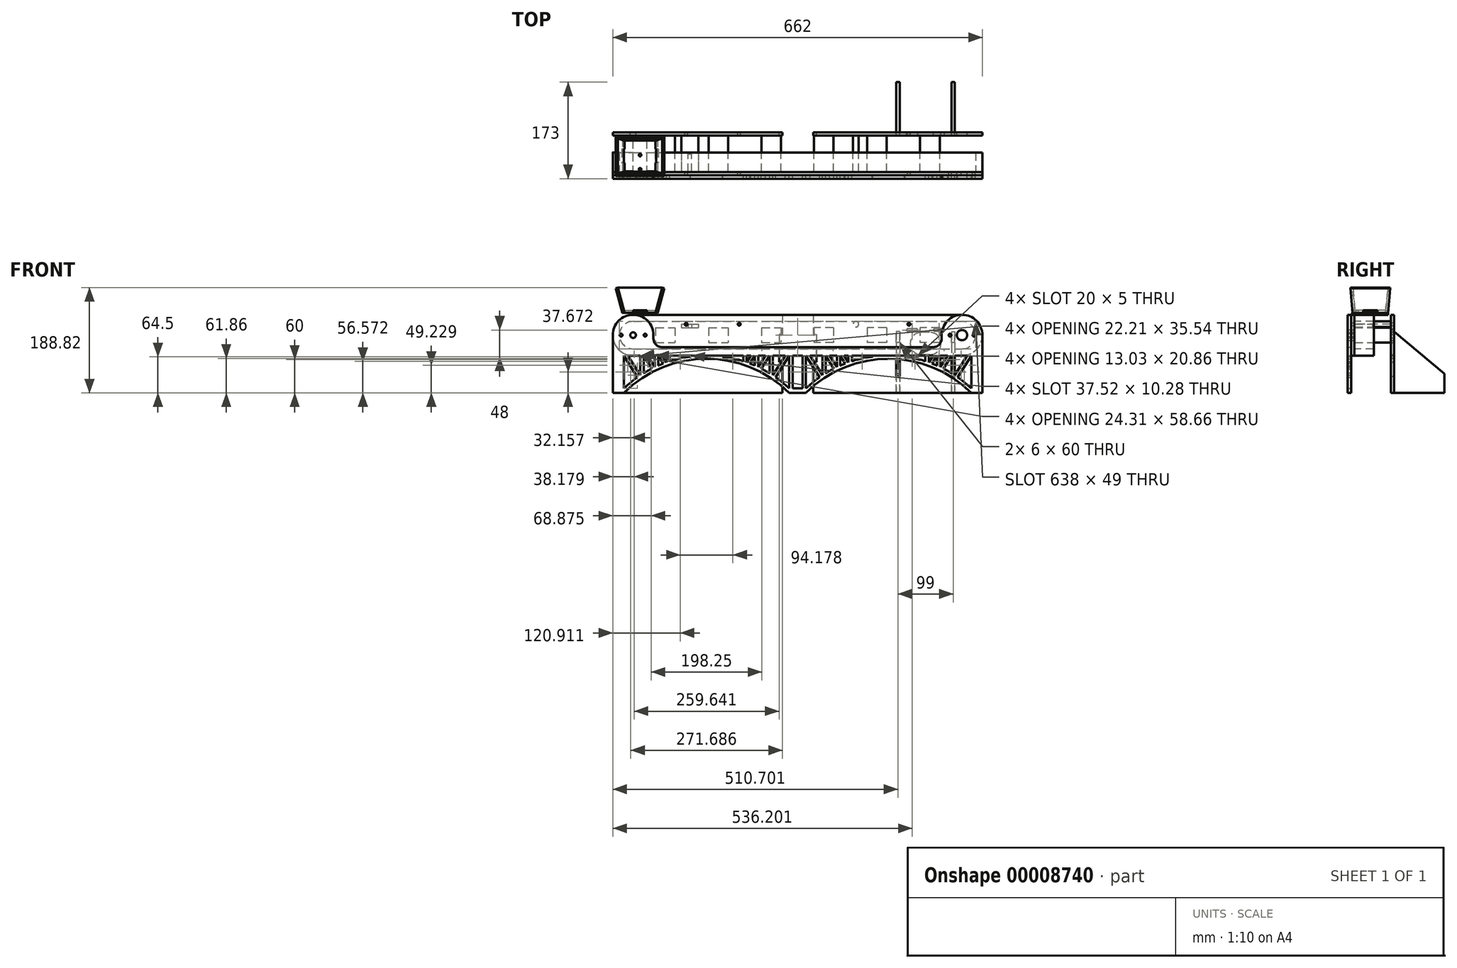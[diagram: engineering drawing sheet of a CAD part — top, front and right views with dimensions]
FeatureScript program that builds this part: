
annotation { "Feature Type Name" : "Feature", "Feature Type Description" : "" }
export const myFeature = defineFeature(function(context is Context, id is Id, definition is map)
    precondition{}
    {
        {
            var Q0;
            Q0=qCreatedBy(makeId("Front.planeOp"),FACE);
            var sketch = newSketch(context, id + "F0", { "sketchPlane" : qUnion([Q0])});
            skLineSegment(sketch, "E0.bottom", {"start": v(331, 0) * mm, "end": v(-331, 0) * mm, "construction": true});
            skLineSegment(sketch, "E0.top", {"start": v(331, 140) * mm, "end": v(-331, 140) * mm, "construction": true});
            skLineSegment(sketch, "E0.left", {"start": v(331, 0) * mm, "end": v(331, 140) * mm, "construction": true});
            skLineSegment(sketch, "E0.right", {"start": v(-331, 0) * mm, "end": v(-331, 140) * mm, "construction": true});
            skCircle(sketch, "E1", {"center": v(-294.5, 103.5) * mm, "radius": 36.5 * mm, "construction": true});
            skCircle(sketch, "E2", {"center": v(-294.5, 103.5) * mm, "radius": 24.5 * mm, "construction": true});
            skLineSegment(sketch, "E3", {"start": v(0, 0) * mm, "end": v(0, 140) * mm, "construction": true});
            skCircle(sketch, "E4.0.MirrorC", {"center": v(294.5, 103.5) * mm, "radius": 36.5 * mm, "construction": true});
            skCircle(sketch, "E5.0.MirrorC", {"center": v(294.5, 103.5) * mm, "radius": 24.5 * mm, "construction": true});
            skLineSegment(sketch, "E6", {"start": v(-294.5, 128) * mm, "end": v(294.5, 128) * mm, "construction": true});
            skCircle(sketch, "E7", {"center": v(-199.5, 123) * mm, "radius": 5 * mm, "construction": true});
            skCircle(sketch, "E8", {"center": v(-104.5, 123) * mm, "radius": 5 * mm, "construction": true});
            skLineSegment(sketch, "E9.left", {"start": v(-27, 0) * mm, "end": v(-27, 140) * mm, "construction": true});
            skLineSegment(sketch, "E9.right", {"start": v(28, 0) * mm, "end": v(28, 140) * mm, "construction": true});
            skLineSegment(sketch, "E10", {"start": v(-33, 0) * mm, "end": v(-33, 140) * mm, "construction": true});
            skLineSegment(sketch, "E11", {"start": v(34, 0) * mm, "end": v(34, 140) * mm, "construction": true});
            skCircle(sketch, "E12.0.MirrorC", {"center": v(199.5, 123) * mm, "radius": 5 * mm, "construction": true});
            skCircle(sketch, "E13.0.MirrorC", {"center": v(104.5, 123) * mm, "radius": 5 * mm, "construction": true});
            skSolve(sketch);
        }
        {
            var Q0;
            Q0=qCreatedBy(makeId("Front.planeOp"),FACE);
            var sketch = newSketch(context, id + "F1", { "sketchPlane" : qUnion([Q0])});
            skLineSegment(sketch, "E14.right", {"start": v(331, 0) * mm, "end": v(331, 103.5) * mm});
            skCircle(sketch, "E15", {"center": v(104.5, 123) * mm, "radius": 2.5 * mm});
            skArc(sketch, "E16", {"start": v(331, 103.5) * mm, "mid": v(320.3, 129.3) * mm, "end": v(294.5, 140) * mm});
            skCircle(sketch, "E17", {"center": v(294.5, 103.5) * mm, "radius": 9.25 * mm});
            skLineSegment(sketch, "E18", {"start": v(331, 0) * mm, "end": v(28, 0) * mm});
            skLineSegment(sketch, "E19", {"start": v(28, 140) * mm, "end": v(28, 105) * mm});
            skLineSegment(sketch, "E20", {"start": v(294.5, 140) * mm, "end": v(28, 140) * mm});
            skCircle(sketch, "E21", {"center": v(199.5, 123) * mm, "radius": 2.5 * mm});
            skLineSegment(sketch, "E22", {"start": v(0, 129.79) * mm, "end": v(0, 0) * mm, "construction": true});
            skLineSegment(sketch, "E23.0.MirrorCS", {"start": v(-294.5, 140) * mm, "end": v(-27, 140) * mm});
            skLineSegment(sketch, "E24.0.MirrorCS", {"start": v(-27, 140) * mm, "end": v(-27, 105) * mm});
            skLineSegment(sketch, "E25.0.MirrorCS", {"start": v(-331, 0) * mm, "end": v(-27, 0) * mm});
            skLineSegment(sketch, "E26.0.MirrorCS", {"start": v(-331, 0) * mm, "end": v(-331, 103.5) * mm});
            skCircle(sketch, "E27.0.MirrorC", {"center": v(-294.5, 103.5) * mm, "radius": 5 * mm});
            skCircle(sketch, "E28.0.MirrorC", {"center": v(-199.5, 123) * mm, "radius": 2.5 * mm});
            skCircle(sketch, "E29.0.MirrorC", {"center": v(-104.5, 123) * mm, "radius": 2.5 * mm});
            skArc(sketch, "E30.0.MirrorCS", {"start": v(-331, 103.5) * mm, "mid": v(-320.3, 129.3) * mm, "end": v(-294.5, 140) * mm});
            skLineSegment(sketch, "E31.bottom", {"start": v(-27, 105) * mm, "end": v(-33, 105) * mm});
            skLineSegment(sketch, "E31.top", {"start": v(-27, 55) * mm, "end": v(-33, 55) * mm});
            skLineSegment(sketch, "E31.right", {"start": v(-33, 105) * mm, "end": v(-33, 55) * mm});
            skLineSegment(sketch, "E32.trimOffspring", {"start": v(-27, 55) * mm, "end": v(-27, 0) * mm});
            skLineSegment(sketch, "E33", {"start": v(28, 105) * mm, "end": v(34, 105) * mm});
            skLineSegment(sketch, "E34", {"start": v(34, 105) * mm, "end": v(34, 55) * mm});
            skLineSegment(sketch, "E35", {"start": v(34, 55) * mm, "end": v(28, 55) * mm});
            skLineSegment(sketch, "E36.trimOffspring", {"start": v(28, 55) * mm, "end": v(28, 0) * mm});
            skArc(sketch, "E37", {"start": v(236.7, 68.5) * mm, "mid": v(256.7, 88.5) * mm, "end": v(236.7, 108.5) * mm});
            skLineSegment(sketch, "E38", {"start": v(294.5, 79) * mm, "end": v(75.4, 79) * mm, "construction": true});
            skArc(sketch, "E39", {"start": v(260.7, 110) * mm, "mid": v(263.2, 112.5) * mm, "end": v(260.7, 115) * mm});
            skArc(sketch, "E40", {"start": v(212.7, 110) * mm, "mid": v(215.2, 112.5) * mm, "end": v(212.7, 115) * mm});
            skArc(sketch, "E41", {"start": v(212.7, 62) * mm, "mid": v(215.2, 64.5) * mm, "end": v(212.7, 67) * mm});
            skLineSegment(sketch, "E42", {"start": v(260.7, 112.5) * mm, "end": v(212.7, 112.5) * mm, "construction": true});
            skLineSegment(sketch, "E43", {"start": v(212.7, 64.5) * mm, "end": v(260.7, 64.5) * mm, "construction": true});
            skLineSegment(sketch, "E44", {"start": v(260.7, 112.5) * mm, "end": v(260.7, 64.5) * mm, "construction": true});
            skLineSegment(sketch, "E45", {"start": v(212.7, 64.5) * mm, "end": v(212.7, 112.5) * mm, "construction": true});
            skLineSegment(sketch, "E46", {"start": v(260.7, 88.5) * mm, "end": v(212.7, 88.5) * mm, "construction": true});
            skLineSegment(sketch, "E47.bottom", {"start": v(281.7, 90) * mm, "end": v(275.7, 90) * mm});
            skLineSegment(sketch, "E47.top", {"start": v(281.7, 30) * mm, "end": v(275.7, 30) * mm});
            skLineSegment(sketch, "E47.left", {"start": v(281.7, 90) * mm, "end": v(281.7, 30) * mm});
            skLineSegment(sketch, "E47.right", {"start": v(275.7, 90) * mm, "end": v(275.7, 30) * mm});
            skLineSegment(sketch, "E48", {"start": v(236.7, 88.5) * mm, "end": v(236.7, 68.5) * mm, "construction": true});
            skLineSegment(sketch, "E49.0.MirrorCS", {"start": v(182.7, 90) * mm, "end": v(182.7, 30) * mm});
            skLineSegment(sketch, "E50.0.MirrorCS", {"start": v(176.7, 90) * mm, "end": v(182.7, 90) * mm});
            skLineSegment(sketch, "E51.0.MirrorCS", {"start": v(176.7, 90) * mm, "end": v(176.7, 30) * mm});
            skLineSegment(sketch, "E52.0.MirrorCS", {"start": v(176.7, 30) * mm, "end": v(182.7, 30) * mm});
            skLineSegment(sketch, "E53", {"start": v(236.7, 108.5) * mm, "end": v(221.7, 108.5) * mm});
            skLineSegment(sketch, "E54", {"start": v(236.7, 68.5) * mm, "end": v(221.7, 68.5) * mm});
            skLineSegment(sketch, "E55", {"start": v(260.7, 115) * mm, "end": v(245.7, 115) * mm});
            skLineSegment(sketch, "E56", {"start": v(260.7, 110) * mm, "end": v(245.7, 110) * mm});
            skLineSegment(sketch, "E57", {"start": v(212.7, 115) * mm, "end": v(197.7, 115) * mm});
            skLineSegment(sketch, "E58", {"start": v(212.7, 110) * mm, "end": v(197.7, 110) * mm});
            skLineSegment(sketch, "E59", {"start": v(260.7, 62) * mm, "end": v(245.7, 62) * mm});
            skLineSegment(sketch, "E60", {"start": v(260.7, 67) * mm, "end": v(245.7, 67) * mm});
            skLineSegment(sketch, "E61", {"start": v(212.7, 62) * mm, "end": v(197.7, 62) * mm});
            skLineSegment(sketch, "E62", {"start": v(212.7, 67) * mm, "end": v(197.7, 67) * mm});
            skArc(sketch, "E63", {"start": v(245.7, 115) * mm, "mid": v(243.2, 112.5) * mm, "end": v(245.7, 110) * mm});
            skArc(sketch, "E64", {"start": v(197.7, 115) * mm, "mid": v(195.2, 112.5) * mm, "end": v(197.7, 110) * mm});
            skArc(sketch, "E65", {"start": v(197.7, 67) * mm, "mid": v(195.2, 64.5) * mm, "end": v(197.7, 62) * mm});
            skArc(sketch, "E66", {"start": v(245.7, 67) * mm, "mid": v(243.2, 64.5) * mm, "end": v(245.7, 62) * mm});
            skArc(sketch, "E67.trimOffspring", {"start": v(260.7, 62) * mm, "mid": v(263.2, 64.5) * mm, "end": v(260.7, 67) * mm});
            skArc(sketch, "E68", {"start": v(221.7, 108.5) * mm, "mid": v(201.7, 88.5) * mm, "end": v(221.7, 68.5) * mm});
            skLineSegment(sketch, "E69", {"start": v(275.7, 90) * mm, "end": v(260.7, 90) * mm, "construction": true});
            skLineSegment(sketch, "E70", {"start": v(182.7, 90) * mm, "end": v(197.7, 90) * mm, "construction": true});
            skLineSegment(sketch, "E71", {"start": v(229.2, 68.5) * mm, "end": v(229.2, 88.5) * mm, "construction": true});
            skSolve(sketch);
        }
        {
            var Q0;
            Q0 = qSketchRegion(id + "F1", true);
            extrude(context, id + "F2", {"entities" : qUnion([Q0]), "depth" : 6 * mm});
        }
        {
            var Q0;
            Q0=makeQuery(id+"F2.opExtrude","CAP_FACE",FACE,{"disambiguationData":[OSD([sQuery(id+"F1.wireOp",EDGE,"E23.0.MirrorCS"),sQuery(id+"F1.wireOp",EDGE,"E24.0.MirrorCS"),sQuery(id+"F1.wireOp",EDGE,"E25.0.MirrorCS"),sQuery(id+"F1.wireOp",EDGE,"E26.0.MirrorCS"),sQuery(id+"F1.wireOp",EDGE,"E27.0.MirrorC"),sQuery(id+"F1.wireOp",EDGE,"E28.0.MirrorC"),sQuery(id+"F1.wireOp",EDGE,"E29.0.MirrorC"),sQuery(id+"F1.wireOp",EDGE,"E30.0.MirrorCS"),sQuery(id+"F1.wireOp",EDGE,"E31.bottom"),sQuery(id+"F1.wireOp",EDGE,"E31.top"),sQuery(id+"F1.wireOp",EDGE,"E31.right"),sQuery(id+"F1.wireOp",EDGE,"E32.trimOffspring")])],"isStart":false});
            var sketch = newSketch(context, id + "F3", { "sketchPlane" : qUnion([Q0])});
            skLineSegment(sketch, "E72.bottom", {"start": v(-254.5, 117) * mm, "end": v(-219.5, 117) * mm});
            skLineSegment(sketch, "E72.top", {"start": v(-254.5, 90) * mm, "end": v(-219.5, 90) * mm});
            skLineSegment(sketch, "E72.left", {"start": v(-254.5, 117) * mm, "end": v(-254.5, 90) * mm});
            skLineSegment(sketch, "E72.right", {"start": v(-219.5, 117) * mm, "end": v(-219.5, 90) * mm});
            skLineSegment(sketch, "E73.bottom", {"start": v(-64.5, 117) * mm, "end": v(-29.5, 117) * mm});
            skLineSegment(sketch, "E73.top", {"start": v(-64.5, 90) * mm, "end": v(-29.5, 90) * mm});
            skLineSegment(sketch, "E73.left", {"start": v(-64.5, 117) * mm, "end": v(-64.5, 90) * mm});
            skLineSegment(sketch, "E73.right", {"start": v(-29.5, 117) * mm, "end": v(-29.5, 90) * mm});
            skLineSegment(sketch, "E74.bottom", {"start": v(-159.5, 117) * mm, "end": v(-124.5, 117) * mm});
            skLineSegment(sketch, "E74.top", {"start": v(-159.5, 90) * mm, "end": v(-124.5, 90) * mm});
            skLineSegment(sketch, "E74.left", {"start": v(-159.5, 117) * mm, "end": v(-159.5, 90) * mm});
            skLineSegment(sketch, "E74.right", {"start": v(-124.5, 117) * mm, "end": v(-124.5, 90) * mm});
            skLineSegment(sketch, "E75", {"start": v(-254.5, 103.5) * mm, "end": v(-29.5, 103.5) * mm, "construction": true});
            skSolve(sketch);
        }
        {
            var Q0;
            Q0 = qSketchRegion(id + "F3", true);
            extrude(context, id + "F4", {"entities" : qUnion([Q0]), "depth" : 65 * mm});
        }
        {
            var Q0;
            Q0=makeQuery(id+"F4.opExtrude","CAP_FACE",FACE,{"disambiguationData":[OSD([sQuery(id+"F3.wireOp",EDGE,"E72.bottom"),sQuery(id+"F3.wireOp",EDGE,"E72.top"),sQuery(id+"F3.wireOp",EDGE,"E72.left"),sQuery(id+"F3.wireOp",EDGE,"E72.right")])],"isStart":false});
            var sketch = newSketch(context, id + "F5", { "sketchPlane" : qUnion([Q0])});
            skLineSegment(sketch, "E76.0.0", {"start": v(-27, 140) * mm, "end": v(-294.5, 140) * mm});
            skArc(sketch, "E76.0.1", {"start": v(-294.5, 140) * mm, "mid": v(-320.3, 129.3) * mm, "end": v(-331, 103.5) * mm});
            skCircle(sketch, "E77.0", {"center": v(-294.5, 103.5) * mm, "radius": 5 * mm});
            skCircle(sketch, "E77.1", {"center": v(-199.5, 123) * mm, "radius": 2.5 * mm});
            skCircle(sketch, "E77.2", {"center": v(-104.5, 123) * mm, "radius": 2.5 * mm});
            skLineSegment(sketch, "E78.0.1", {"start": v(331, 0) * mm, "end": v(331, 103.5) * mm, "construction": true});
            skArc(sketch, "E78.0.2", {"start": v(331, 103.5) * mm, "mid": v(320.3, 129.3) * mm, "end": v(294.5, 140) * mm});
            skLineSegment(sketch, "E78.0.3", {"start": v(294.5, 140) * mm, "end": v(28, 140) * mm});
            skCircle(sketch, "E79.0", {"center": v(104.5, 123) * mm, "radius": 2.5 * mm});
            skCircle(sketch, "E79.1", {"center": v(199.5, 123) * mm, "radius": 2.5 * mm});
            skCircle(sketch, "E79.2", {"center": v(294.5, 103.5) * mm, "radius": 9.25 * mm});
            skLineSegment(sketch, "E80", {"start": v(-27, 140) * mm, "end": v(28, 140) * mm});
            skLineSegment(sketch, "E81", {"start": v(311, 0) * mm, "end": v(331, 0) * mm, "construction": true});
            skLineSegment(sketch, "E82", {"start": v(-15, 0) * mm, "end": v(15, 0) * mm, "construction": true});
            skPoint(sketch, "E83.visualSharp", {"position": v(0, 67) * mm});
            skArc(sketch, "E84", {"start": v(-15, 0) * mm, "mid": v(-163, 61) * mm, "end": v(-311, 0) * mm, "construction": true});
            skLineSegment(sketch, "E85", {"start": v(-311, 0) * mm, "end": v(-331, 0) * mm, "construction": true});
            skLineSegment(sketch, "E86", {"start": v(-292.82, 67) * mm, "end": v(0, 67) * mm});
            skArc(sketch, "E87.0", {"start": v(-15, 8.34) * mm, "mid": v(-26.8, 18.66) * mm, "end": v(-39.31, 28.1) * mm, "construction": true});
            skLineSegment(sketch, "E88", {"start": v(-311, 8.34) * mm, "end": v(-311, 67) * mm, "construction": true});
            skLineSegment(sketch, "E89", {"start": v(-311, 67) * mm, "end": v(-286.69, 28.1) * mm, "construction": true});
            skLineSegment(sketch, "E90", {"start": v(-281.72, 31.46) * mm, "end": v(-303.92, 67) * mm, "construction": true});
            skLineSegment(sketch, "E91", {"start": v(-303.92, 67) * mm, "end": v(-281.72, 67) * mm, "construction": true});
            skLineSegment(sketch, "E92", {"start": v(-281.72, 67) * mm, "end": v(-281.72, 31.46) * mm, "construction": true});
            skLineSegment(sketch, "E93", {"start": v(-275.72, 35.27) * mm, "end": v(-275.72, 67) * mm, "construction": true});
            skLineSegment(sketch, "E94", {"start": v(-275.72, 67) * mm, "end": v(-261.02, 43.48) * mm, "construction": true});
            skLineSegment(sketch, "E95", {"start": v(-268.64, 67) * mm, "end": v(-255.6, 46.14) * mm, "construction": true});
            skLineSegment(sketch, "E96", {"start": v(-255.6, 46.14) * mm, "end": v(-255.6, 67) * mm, "construction": true});
            skLineSegment(sketch, "E97", {"start": v(-255.6, 67) * mm, "end": v(-268.64, 67) * mm, "construction": true});
            skLineSegment(sketch, "E98", {"start": v(-249.6, 48.88) * mm, "end": v(-249.6, 67) * mm, "construction": true});
            skLineSegment(sketch, "E99", {"start": v(-249.6, 67) * mm, "end": v(-240.6, 52.58) * mm, "construction": true});
            skLineSegment(sketch, "E100", {"start": v(-234.85, 54.7) * mm, "end": v(-242.53, 67) * mm, "construction": true});
            skLineSegment(sketch, "E101", {"start": v(-242.53, 67) * mm, "end": v(-234.85, 67) * mm, "construction": true});
            skLineSegment(sketch, "E102", {"start": v(-234.85, 67) * mm, "end": v(-234.85, 54.7) * mm, "construction": true});
            skLineSegment(sketch, "E103", {"start": v(-228.85, 56.72) * mm, "end": v(-228.85, 67) * mm, "construction": true});
            skLineSegment(sketch, "E104", {"start": v(-228.85, 67) * mm, "end": v(-192.33, 67) * mm, "construction": true});
            skArc(sketch, "E105.trimOffspring", {"start": v(-286.69, 28.1) * mm, "mid": v(-299.2, 18.66) * mm, "end": v(-311, 8.34) * mm, "construction": true});
            skArc(sketch, "E106.trimOffspring", {"start": v(-261.02, 43.48) * mm, "mid": v(-268.45, 39.52) * mm, "end": v(-275.72, 35.27) * mm, "construction": true});
            skArc(sketch, "E107.trimOffspring", {"start": v(-240.6, 52.58) * mm, "mid": v(-245.13, 50.78) * mm, "end": v(-249.6, 48.88) * mm, "construction": true});
            skArc(sketch, "E108.trimOffspring", {"start": v(-192.33, 65) * mm, "mid": v(-210.77, 61.65) * mm, "end": v(-228.85, 56.72) * mm, "construction": true});
            skLineSegment(sketch, "E109", {"start": v(-163, 67) * mm, "end": v(-163, -25.9) * mm, "construction": true});
            skLineSegment(sketch, "E110.0.MirrorCS", {"start": v(-15, 8.34) * mm, "end": v(-15, 67) * mm, "construction": true});
            skLineSegment(sketch, "E111.0.MirrorCS", {"start": v(-15, 67) * mm, "end": v(-39.31, 28.1) * mm, "construction": true});
            skLineSegment(sketch, "E112.0.MirrorCS", {"start": v(-44.28, 31.46) * mm, "end": v(-22.08, 67) * mm, "construction": true});
            skLineSegment(sketch, "E113.0.MirrorCS", {"start": v(-22.08, 67) * mm, "end": v(-44.28, 67) * mm, "construction": true});
            skLineSegment(sketch, "E114.0.MirrorCS", {"start": v(-44.28, 67) * mm, "end": v(-44.28, 31.46) * mm, "construction": true});
            skLineSegment(sketch, "E115.0.MirrorCS", {"start": v(-50.28, 35.27) * mm, "end": v(-50.28, 67) * mm, "construction": true});
            skLineSegment(sketch, "E116.0.MirrorCS", {"start": v(-50.28, 67) * mm, "end": v(-64.98, 43.48) * mm, "construction": true});
            skLineSegment(sketch, "E117.0.MirrorCS", {"start": v(-70.4, 67) * mm, "end": v(-57.36, 67) * mm, "construction": true});
            skLineSegment(sketch, "E118.0.MirrorCS", {"start": v(-57.36, 67) * mm, "end": v(-70.4, 46.14) * mm, "construction": true});
            skLineSegment(sketch, "E119.0.MirrorCS", {"start": v(-70.4, 46.14) * mm, "end": v(-70.4, 67) * mm, "construction": true});
            skLineSegment(sketch, "E120.0.MirrorCS", {"start": v(-76.4, 67) * mm, "end": v(-85.4, 52.58) * mm, "construction": true});
            skLineSegment(sketch, "E121.0.MirrorCS", {"start": v(-76.4, 48.88) * mm, "end": v(-76.4, 67) * mm, "construction": true});
            skLineSegment(sketch, "E122.0.MirrorCS", {"start": v(-83.47, 67) * mm, "end": v(-91.15, 67) * mm, "construction": true});
            skLineSegment(sketch, "E123.0.MirrorCS", {"start": v(-91.15, 54.7) * mm, "end": v(-83.47, 67) * mm, "construction": true});
            skLineSegment(sketch, "E124.0.MirrorCS", {"start": v(-91.15, 67) * mm, "end": v(-91.15, 54.7) * mm, "construction": true});
            skLineSegment(sketch, "E125.0.MirrorCS", {"start": v(-97.15, 67) * mm, "end": v(-133.67, 67) * mm, "construction": true});
            skLineSegment(sketch, "E126.0.MirrorCS", {"start": v(-97.15, 56.72) * mm, "end": v(-97.15, 67) * mm, "construction": true});
            skArc(sketch, "E127.trimOffspring", {"start": v(-50.28, 35.27) * mm, "mid": v(-57.55, 39.52) * mm, "end": v(-64.98, 43.48) * mm, "construction": true});
            skArc(sketch, "E128.trimOffspring", {"start": v(-76.4, 48.88) * mm, "mid": v(-80.87, 50.78) * mm, "end": v(-85.4, 52.58) * mm, "construction": true});
            skArc(sketch, "E129.trimOffspring", {"start": v(-97.15, 56.72) * mm, "mid": v(-115.36, 61.68) * mm, "end": v(-133.94, 65.04) * mm, "construction": true});
            skLineSegment(sketch, "E130", {"start": v(0, 0) * mm, "end": v(0, -72.45) * mm, "construction": true});
            skArc(sketch, "E131.0.MirrorCS", {"start": v(240.6, 52.58) * mm, "mid": v(245.13, 50.78) * mm, "end": v(249.6, 48.88) * mm, "construction": true});
            skLineSegment(sketch, "E131.1.MirrorCS", {"start": v(234.85, 54.7) * mm, "end": v(242.53, 67) * mm, "construction": true});
            skLineSegment(sketch, "E131.2.MirrorCS", {"start": v(242.53, 67) * mm, "end": v(234.85, 67) * mm, "construction": true});
            skArc(sketch, "E131.3.MirrorCS", {"start": v(76.4, 48.88) * mm, "mid": v(80.87, 50.78) * mm, "end": v(85.4, 52.58) * mm, "construction": true});
            skLineSegment(sketch, "E131.4.MirrorCS", {"start": v(91.15, 54.7) * mm, "end": v(83.47, 67) * mm, "construction": true});
            skLineSegment(sketch, "E131.5.MirrorCS", {"start": v(234.85, 67) * mm, "end": v(234.85, 54.7) * mm, "construction": true});
            skLineSegment(sketch, "E131.6.MirrorCS", {"start": v(91.15, 67) * mm, "end": v(91.15, 54.7) * mm, "construction": true});
            skLineSegment(sketch, "E131.7.MirrorCS", {"start": v(228.85, 56.72) * mm, "end": v(228.85, 67) * mm, "construction": true});
            skLineSegment(sketch, "E131.8.MirrorCS", {"start": v(97.15, 56.72) * mm, "end": v(97.15, 67) * mm, "construction": true});
            skLineSegment(sketch, "E131.9.MirrorCS", {"start": v(83.47, 67) * mm, "end": v(91.15, 67) * mm, "construction": true});
            skLineSegment(sketch, "E131.10.MirrorCS", {"start": v(255.6, 67) * mm, "end": v(268.64, 67) * mm, "construction": true});
            skLineSegment(sketch, "E131.11.MirrorCS", {"start": v(70.4, 67) * mm, "end": v(57.36, 67) * mm, "construction": true});
            skLineSegment(sketch, "E131.12.MirrorCS", {"start": v(15, 8.34) * mm, "end": v(15, 67) * mm, "construction": true});
            skLineSegment(sketch, "E131.13.MirrorCS", {"start": v(303.92, 67) * mm, "end": v(281.72, 67) * mm, "construction": true});
            skLineSegment(sketch, "E131.14.MirrorCS", {"start": v(275.72, 67) * mm, "end": v(261.02, 43.48) * mm, "construction": true});
            skLineSegment(sketch, "E131.15.MirrorCS", {"start": v(50.28, 35.27) * mm, "end": v(50.28, 67) * mm, "construction": true});
            skArc(sketch, "E131.16.MirrorCS", {"start": v(286.69, 28.1) * mm, "mid": v(299.2, 18.66) * mm, "end": v(311, 8.34) * mm, "construction": true});
            skLineSegment(sketch, "E131.17.MirrorCS", {"start": v(44.28, 31.46) * mm, "end": v(22.08, 67) * mm, "construction": true});
            skLineSegment(sketch, "E131.18.MirrorCS", {"start": v(281.72, 31.46) * mm, "end": v(303.92, 67) * mm, "construction": true});
            skArc(sketch, "E131.19.MirrorCS", {"start": v(15, 0) * mm, "mid": v(163, 61) * mm, "end": v(311, 0) * mm, "construction": true});
            skLineSegment(sketch, "E131.20.MirrorCS", {"start": v(249.6, 48.88) * mm, "end": v(249.6, 67) * mm, "construction": true});
            skArc(sketch, "E131.21.MirrorCS", {"start": v(50.28, 35.27) * mm, "mid": v(57.55, 39.52) * mm, "end": v(64.98, 43.48) * mm, "construction": true});
            skLineSegment(sketch, "E131.22.MirrorCS", {"start": v(76.4, 48.88) * mm, "end": v(76.4, 67) * mm, "construction": true});
            skLineSegment(sketch, "E131.23.MirrorCS", {"start": v(76.4, 67) * mm, "end": v(85.4, 52.58) * mm, "construction": true});
            skLineSegment(sketch, "E131.24.MirrorCS", {"start": v(275.72, 35.27) * mm, "end": v(275.72, 67) * mm, "construction": true});
            skArc(sketch, "E131.25.MirrorCS", {"start": v(15, 8.34) * mm, "mid": v(26.8, 18.66) * mm, "end": v(39.31, 28.1) * mm, "construction": true});
            skArc(sketch, "E131.26.MirrorCS", {"start": v(261.02, 43.48) * mm, "mid": v(268.45, 39.52) * mm, "end": v(275.72, 35.27) * mm, "construction": true});
            skLineSegment(sketch, "E131.27.MirrorCS", {"start": v(311, 67) * mm, "end": v(286.69, 28.1) * mm, "construction": true});
            skLineSegment(sketch, "E131.28.MirrorCS", {"start": v(249.6, 67) * mm, "end": v(240.6, 52.58) * mm, "construction": true});
            skLineSegment(sketch, "E131.29.MirrorCS", {"start": v(281.72, 67) * mm, "end": v(281.72, 31.46) * mm, "construction": true});
            skLineSegment(sketch, "E131.30.MirrorCS", {"start": v(22.08, 67) * mm, "end": v(44.28, 67) * mm, "construction": true});
            skLineSegment(sketch, "E131.31.MirrorCS", {"start": v(311, 8.34) * mm, "end": v(311, 67) * mm, "construction": true});
            skArc(sketch, "E131.32.MirrorCS", {"start": v(97.15, 56.72) * mm, "mid": v(115.36, 61.68) * mm, "end": v(133.94, 65.04) * mm, "construction": true});
            skLineSegment(sketch, "E131.33.MirrorCS", {"start": v(228.85, 67) * mm, "end": v(192.33, 67) * mm, "construction": true});
            skLineSegment(sketch, "E131.34.MirrorCS", {"start": v(57.36, 67) * mm, "end": v(70.4, 46.14) * mm, "construction": true});
            skLineSegment(sketch, "E131.35.MirrorCS", {"start": v(255.6, 46.14) * mm, "end": v(255.6, 67) * mm, "construction": true});
            skLineSegment(sketch, "E131.36.MirrorCS", {"start": v(70.4, 46.14) * mm, "end": v(70.4, 67) * mm, "construction": true});
            skLineSegment(sketch, "E131.37.MirrorCS", {"start": v(97.15, 67) * mm, "end": v(133.67, 67) * mm, "construction": true});
            skLineSegment(sketch, "E131.38.MirrorCS", {"start": v(44.28, 67) * mm, "end": v(44.28, 31.46) * mm, "construction": true});
            skLineSegment(sketch, "E131.39.MirrorCS", {"start": v(268.64, 67) * mm, "end": v(255.6, 46.14) * mm, "construction": true});
            skLineSegment(sketch, "E131.40.MirrorCS", {"start": v(15, 67) * mm, "end": v(39.31, 28.1) * mm, "construction": true});
            skLineSegment(sketch, "E131.41.MirrorCS", {"start": v(50.28, 67) * mm, "end": v(64.98, 43.48) * mm, "construction": true});
            skArc(sketch, "E131.43.MirrorCS", {"start": v(192.06, 65.04) * mm, "mid": v(210.64, 61.68) * mm, "end": v(228.85, 56.72) * mm, "construction": true});
            skLineSegment(sketch, "E132", {"start": v(-9, 67) * mm, "end": v(-9, 8.34) * mm, "construction": true});
            skLineSegment(sketch, "E133", {"start": v(-9, 8.34) * mm, "end": v(9, 8.34) * mm, "construction": true});
            skLineSegment(sketch, "E134", {"start": v(9, 8.34) * mm, "end": v(9, 67) * mm, "construction": true});
            skLineSegment(sketch, "E135", {"start": v(9, 67) * mm, "end": v(-9, 67) * mm, "construction": true});
            skArc(sketch, "E136", {"start": v(-192.33, 65) * mm, "mid": v(-191.33, 66) * mm, "end": v(-192.33, 67) * mm, "construction": true});
            skPoint(sketch, "E137.orphan", {"position": v(-163, 67) * mm});
            skArc(sketch, "E138.0.MirrorCS", {"start": v(-133.67, 65) * mm, "mid": v(-134.67, 66) * mm, "end": v(-133.67, 67) * mm, "construction": true});
            skArc(sketch, "E139.0.MirrorCS", {"start": v(133.67, 65) * mm, "mid": v(134.67, 66) * mm, "end": v(133.67, 67) * mm, "construction": true});
            skArc(sketch, "E140.0.MirrorCS", {"start": v(192.33, 65) * mm, "mid": v(191.33, 66) * mm, "end": v(192.33, 67) * mm, "construction": true});
            skPoint(sketch, "E141.orphan", {"position": v(163, 67) * mm});
            skArc(sketch, "E142", {"start": v(-331, 103.5) * mm, "mid": v(-319.71, 77.1) * mm, "end": v(-292.82, 67) * mm});
            skLineSegment(sketch, "E143", {"start": v(0, 67) * mm, "end": v(292.82, 67) * mm});
            skArc(sketch, "E144", {"start": v(292.82, 67) * mm, "mid": v(319.71, 77.1) * mm, "end": v(331, 103.5) * mm});
            skLineSegment(sketch, "E145", {"start": v(-331, 103.5) * mm, "end": v(-258, 103.5) * mm, "construction": true});
            skCircle(sketch, "E146", {"center": v(-316, 103.5) * mm, "radius": 2.5 * mm});
            skCircle(sketch, "E147", {"center": v(-273, 103.5) * mm, "radius": 2.5 * mm});
            skLineSegment(sketch, "E148", {"start": v(331, 103.5) * mm, "end": v(258, 103.5) * mm, "construction": true});
            skCircle(sketch, "E149", {"center": v(273, 103.5) * mm, "radius": 2.5 * mm});
            skCircle(sketch, "E150", {"center": v(316, 103.5) * mm, "radius": 2.5 * mm});
            skSolve(sketch);
        }
        {
            var Q0;
            Q0 = qSketchRegion(id + "F5", true);
            extrude(context, id + "F6", {"entities" : qUnion([Q0]), "depth" : 6 * mm});
        }
        {
            var Q0;
            Q0=makeQuery(id+"F4.opExtrude","SWEPT_BODY",BODY,{"disambiguationData":[OSD([sQuery(id+"F3.wireOp",EDGE,"E72.bottom"),sQuery(id+"F3.wireOp",EDGE,"E72.top"),sQuery(id+"F3.wireOp",EDGE,"E72.left"),sQuery(id+"F3.wireOp",EDGE,"E72.right")])]});
            var Q1;
            Q1=makeQuery(id+"F4.opExtrude","SWEPT_BODY",BODY,{"disambiguationData":[OSD([sQuery(id+"F3.wireOp",EDGE,"E74.bottom"),sQuery(id+"F3.wireOp",EDGE,"E74.top"),sQuery(id+"F3.wireOp",EDGE,"E74.left"),sQuery(id+"F3.wireOp",EDGE,"E74.right")])]});
            var Q2;
            Q2=makeQuery(id+"F4.opExtrude","SWEPT_BODY",BODY,{"disambiguationData":[OSD([sQuery(id+"F3.wireOp",EDGE,"E73.bottom"),sQuery(id+"F3.wireOp",EDGE,"E73.top"),sQuery(id+"F3.wireOp",EDGE,"E73.left"),sQuery(id+"F3.wireOp",EDGE,"E73.right")])]});
            var Q3;
            Q3=qCreatedBy(makeId("Right.planeOp"),FACE);
            mirror(context, id + "F7", {"entities" : qUnion([Q0, Q1, Q2]), "mirrorPlane" : qUnion([Q3])});
        }
        {
            var Q0;
            Q0=makeQuery(id+"F6.opExtrude","CAP_FACE",FACE,{"disambiguationData":[OSD([sQuery(id+"F5.wireOp",EDGE,"E76.0.0"),sQuery(id+"F5.wireOp",EDGE,"E76.0.1"),sQuery(id+"F5.wireOp",EDGE,"E76.0.2"),sQuery(id+"F5.wireOp",EDGE,"E77.0"),sQuery(id+"F5.wireOp",EDGE,"E77.1"),sQuery(id+"F5.wireOp",EDGE,"E77.2"),sQuery(id+"F5.wireOp",EDGE,"E78.0.1"),sQuery(id+"F5.wireOp",EDGE,"E78.0.2"),sQuery(id+"F5.wireOp",EDGE,"E78.0.3"),sQuery(id+"F5.wireOp",EDGE,"E79.0"),sQuery(id+"F5.wireOp",EDGE,"E79.1"),sQuery(id+"F5.wireOp",EDGE,"E79.2"),sQuery(id+"F5.wireOp",EDGE,"E80"),sQuery(id+"F5.wireOp",EDGE,"E81"),sQuery(id+"F5.wireOp",EDGE,"E82"),sQuery(id+"F5.wireOp",EDGE,"E84"),sQuery(id+"F5.wireOp",EDGE,"E85"),sQuery(id+"F5.wireOp",EDGE,"E87.0"),sQuery(id+"F5.wireOp",EDGE,"E88"),sQuery(id+"F5.wireOp",EDGE,"E89"),sQuery(id+"F5.wireOp",EDGE,"E90"),sQuery(id+"F5.wireOp",EDGE,"E91"),sQuery(id+"F5.wireOp",EDGE,"E92"),sQuery(id+"F5.wireOp",EDGE,"E93"),sQuery(id+"F5.wireOp",EDGE,"E94"),sQuery(id+"F5.wireOp",EDGE,"E95"),sQuery(id+"F5.wireOp",EDGE,"E96"),sQuery(id+"F5.wireOp",EDGE,"E97"),sQuery(id+"F5.wireOp",EDGE,"E98"),sQuery(id+"F5.wireOp",EDGE,"E99"),sQuery(id+"F5.wireOp",EDGE,"E100"),sQuery(id+"F5.wireOp",EDGE,"E101"),sQuery(id+"F5.wireOp",EDGE,"E102"),sQuery(id+"F5.wireOp",EDGE,"E103"),sQuery(id+"F5.wireOp",EDGE,"E104"),sQuery(id+"F5.wireOp",EDGE,"E105.trimOffspring"),sQuery(id+"F5.wireOp",EDGE,"E106.trimOffspring"),sQuery(id+"F5.wireOp",EDGE,"E107.trimOffspring"),sQuery(id+"F5.wireOp",EDGE,"E108.trimOffspring"),sQuery(id+"F5.wireOp",EDGE,"E110.0.MirrorCS"),sQuery(id+"F5.wireOp",EDGE,"E111.0.MirrorCS"),sQuery(id+"F5.wireOp",EDGE,"E112.0.MirrorCS"),sQuery(id+"F5.wireOp",EDGE,"E113.0.MirrorCS"),sQuery(id+"F5.wireOp",EDGE,"E114.0.MirrorCS"),sQuery(id+"F5.wireOp",EDGE,"E115.0.MirrorCS"),sQuery(id+"F5.wireOp",EDGE,"E116.0.MirrorCS"),sQuery(id+"F5.wireOp",EDGE,"E117.0.MirrorCS"),sQuery(id+"F5.wireOp",EDGE,"E118.0.MirrorCS"),sQuery(id+"F5.wireOp",EDGE,"E119.0.MirrorCS"),sQuery(id+"F5.wireOp",EDGE,"E120.0.MirrorCS"),sQuery(id+"F5.wireOp",EDGE,"E121.0.MirrorCS"),sQuery(id+"F5.wireOp",EDGE,"E122.0.MirrorCS"),sQuery(id+"F5.wireOp",EDGE,"E123.0.MirrorCS"),sQuery(id+"F5.wireOp",EDGE,"E124.0.MirrorCS"),sQuery(id+"F5.wireOp",EDGE,"E125.0.MirrorCS"),sQuery(id+"F5.wireOp",EDGE,"E126.0.MirrorCS"),sQuery(id+"F5.wireOp",EDGE,"E127.trimOffspring"),sQuery(id+"F5.wireOp",EDGE,"E128.trimOffspring"),sQuery(id+"F5.wireOp",EDGE,"E129.trimOffspring"),sQuery(id+"F5.wireOp",EDGE,"E131.0.MirrorCS"),sQuery(id+"F5.wireOp",EDGE,"E131.1.MirrorCS"),sQuery(id+"F5.wireOp",EDGE,"E131.2.MirrorCS"),sQuery(id+"F5.wireOp",EDGE,"E131.3.MirrorCS"),sQuery(id+"F5.wireOp",EDGE,"E131.4.MirrorCS"),sQuery(id+"F5.wireOp",EDGE,"E131.5.MirrorCS"),sQuery(id+"F5.wireOp",EDGE,"E131.6.MirrorCS"),sQuery(id+"F5.wireOp",EDGE,"E131.7.MirrorCS"),sQuery(id+"F5.wireOp",EDGE,"E131.8.MirrorCS"),sQuery(id+"F5.wireOp",EDGE,"E131.9.MirrorCS"),sQuery(id+"F5.wireOp",EDGE,"E131.10.MirrorCS"),sQuery(id+"F5.wireOp",EDGE,"E131.11.MirrorCS"),sQuery(id+"F5.wireOp",EDGE,"E131.12.MirrorCS"),sQuery(id+"F5.wireOp",EDGE,"E131.13.MirrorCS"),sQuery(id+"F5.wireOp",EDGE,"E131.14.MirrorCS"),sQuery(id+"F5.wireOp",EDGE,"E131.15.MirrorCS"),sQuery(id+"F5.wireOp",EDGE,"E131.16.MirrorCS"),sQuery(id+"F5.wireOp",EDGE,"E131.17.MirrorCS"),sQuery(id+"F5.wireOp",EDGE,"E131.18.MirrorCS"),sQuery(id+"F5.wireOp",EDGE,"E131.20.MirrorCS"),sQuery(id+"F5.wireOp",EDGE,"E131.21.MirrorCS"),sQuery(id+"F5.wireOp",EDGE,"E131.22.MirrorCS"),sQuery(id+"F5.wireOp",EDGE,"E131.23.MirrorCS"),sQuery(id+"F5.wireOp",EDGE,"E131.24.MirrorCS"),sQuery(id+"F5.wireOp",EDGE,"E131.25.MirrorCS"),sQuery(id+"F5.wireOp",EDGE,"E131.26.MirrorCS"),sQuery(id+"F5.wireOp",EDGE,"E131.27.MirrorCS"),sQuery(id+"F5.wireOp",EDGE,"E131.28.MirrorCS"),sQuery(id+"F5.wireOp",EDGE,"E131.29.MirrorCS"),sQuery(id+"F5.wireOp",EDGE,"E131.30.MirrorCS"),sQuery(id+"F5.wireOp",EDGE,"E131.31.MirrorCS"),sQuery(id+"F5.wireOp",EDGE,"E131.32.MirrorCS"),sQuery(id+"F5.wireOp",EDGE,"E131.33.MirrorCS"),sQuery(id+"F5.wireOp",EDGE,"E131.34.MirrorCS"),sQuery(id+"F5.wireOp",EDGE,"E131.35.MirrorCS"),sQuery(id+"F5.wireOp",EDGE,"E131.36.MirrorCS"),sQuery(id+"F5.wireOp",EDGE,"E131.37.MirrorCS"),sQuery(id+"F5.wireOp",EDGE,"E131.38.MirrorCS"),sQuery(id+"F5.wireOp",EDGE,"E131.39.MirrorCS"),sQuery(id+"F5.wireOp",EDGE,"E131.40.MirrorCS"),sQuery(id+"F5.wireOp",EDGE,"E131.41.MirrorCS"),sQuery(id+"F5.wireOp",EDGE,"E131.43.MirrorCS"),sQuery(id+"F5.wireOp",EDGE,"E131.19.MirrorCS"),sQuery(id+"F5.wireOp",EDGE,"E132"),sQuery(id+"F5.wireOp",EDGE,"E133"),sQuery(id+"F5.wireOp",EDGE,"E134"),sQuery(id+"F5.wireOp",EDGE,"E135"),sQuery(id+"F5.wireOp",EDGE,"E136"),sQuery(id+"F5.wireOp",EDGE,"E138.0.MirrorCS"),sQuery(id+"F5.wireOp",EDGE,"E139.0.MirrorCS"),sQuery(id+"F5.wireOp",EDGE,"E140.0.MirrorCS")])],"isStart":true});
            var sketch = newSketch(context, id + "F8", { "sketchPlane" : qUnion([Q0])});
            skLineSegment(sketch, "E151.0", {"start": v(294.5, 128) * mm, "end": v(-294.5, 128) * mm});
            skArc(sketch, "E151.1", {"start": v(294.5, 128) * mm, "mid": v(319, 103.5) * mm, "end": v(294.5, 79) * mm});
            skArc(sketch, "E151.2", {"start": v(294.5, 140) * mm, "mid": v(331, 103.5) * mm, "end": v(294.5, 67) * mm});
            skLineSegment(sketch, "E151.3", {"start": v(-294.5, 140) * mm, "end": v(294.5, 140) * mm});
            skArc(sketch, "E151.4", {"start": v(-294.5, 140) * mm, "mid": v(-331, 103.5) * mm, "end": v(-294.5, 67) * mm});
            skArc(sketch, "E151.5", {"start": v(-294.5, 128) * mm, "mid": v(-319, 103.5) * mm, "end": v(-294.5, 79) * mm});
            skLineSegment(sketch, "E152", {"start": v(294.5, 67) * mm, "end": v(-294.5, 67) * mm});
            skLineSegment(sketch, "E153", {"start": v(294.5, 79) * mm, "end": v(-294.5, 79) * mm});
            skPoint(sketch, "E154.orphan", {"position": v(331, 140) * mm});
            skPoint(sketch, "E155.orphan", {"position": v(-331, 140) * mm});
            skSolve(sketch);
        }
        {
            var Q0;
            Q0 = qSketchRegion(id + "F8", true);
            extrude(context, id + "F9", {"entities" : qUnion([Q0]), "depth" : 35 * mm});
        }
        {
            var Q0;
            Q0=makeQuery(id+"F6.opExtrude","CAP_FACE",FACE,{"disambiguationData":[OSD([sQuery(id+"F5.wireOp",EDGE,"E76.0.0"),sQuery(id+"F5.wireOp",EDGE,"E76.0.1"),sQuery(id+"F5.wireOp",EDGE,"E77.0"),sQuery(id+"F5.wireOp",EDGE,"E77.1"),sQuery(id+"F5.wireOp",EDGE,"E77.2"),sQuery(id+"F5.wireOp",EDGE,"E78.0.2"),sQuery(id+"F5.wireOp",EDGE,"E78.0.3"),sQuery(id+"F5.wireOp",EDGE,"E79.0"),sQuery(id+"F5.wireOp",EDGE,"E79.1"),sQuery(id+"F5.wireOp",EDGE,"E79.2"),sQuery(id+"F5.wireOp",EDGE,"E80"),sQuery(id+"F5.wireOp",EDGE,"E86"),sQuery(id+"F5.wireOp",EDGE,"E142"),sQuery(id+"F5.wireOp",EDGE,"E143"),sQuery(id+"F5.wireOp",EDGE,"E144")])],"isStart":false});
            var sketch = newSketch(context, id + "F10", { "sketchPlane" : qUnion([Q0])});
            skLineSegment(sketch, "E156.0", {"start": v(-311, 8.34) * mm, "end": v(-311, 67) * mm});
            skLineSegment(sketch, "E157.0", {"start": v(-311, 67) * mm, "end": v(-286.69, 28.1) * mm});
            skLineSegment(sketch, "E158.0", {"start": v(-281.72, 31.46) * mm, "end": v(-303.92, 67) * mm});
            skLineSegment(sketch, "E159.0", {"start": v(-281.72, 67) * mm, "end": v(-281.72, 31.46) * mm});
            skLineSegment(sketch, "E160.0", {"start": v(-275.72, 35.27) * mm, "end": v(-275.72, 67) * mm});
            skLineSegment(sketch, "E161.0", {"start": v(-275.72, 67) * mm, "end": v(-261.02, 43.48) * mm});
            skLineSegment(sketch, "E162.0", {"start": v(-268.64, 67) * mm, "end": v(-255.6, 46.14) * mm});
            skLineSegment(sketch, "E163.0", {"start": v(-255.6, 46.14) * mm, "end": v(-255.6, 67) * mm});
            skLineSegment(sketch, "E164.0", {"start": v(-249.6, 48.88) * mm, "end": v(-249.6, 67) * mm});
            skLineSegment(sketch, "E165.0", {"start": v(-249.6, 67) * mm, "end": v(-240.6, 52.58) * mm});
            skLineSegment(sketch, "E166.0", {"start": v(-234.85, 54.7) * mm, "end": v(-242.53, 67) * mm});
            skLineSegment(sketch, "E167.0", {"start": v(-234.85, 67) * mm, "end": v(-234.85, 54.7) * mm});
            skLineSegment(sketch, "E168.0", {"start": v(-228.85, 56.72) * mm, "end": v(-228.85, 67) * mm});
            skArc(sketch, "E169.0", {"start": v(-192.33, 65) * mm, "mid": v(-210.77, 61.65) * mm, "end": v(-228.85, 56.72) * mm});
            skArc(sketch, "E170.0", {"start": v(-286.69, 28.1) * mm, "mid": v(-299.2, 18.66) * mm, "end": v(-311, 8.34) * mm});
            skArc(sketch, "E171.0", {"start": v(-261.02, 43.48) * mm, "mid": v(-268.45, 39.52) * mm, "end": v(-275.72, 35.27) * mm});
            skArc(sketch, "E172.0", {"start": v(-240.6, 52.58) * mm, "mid": v(-245.13, 50.78) * mm, "end": v(-249.6, 48.88) * mm});
            skArc(sketch, "E173.0", {"start": v(-15, 0) * mm, "mid": v(-163, 61) * mm, "end": v(-311, 0) * mm});
            skLineSegment(sketch, "E174.0", {"start": v(-311, 0) * mm, "end": v(-331, 0) * mm});
            skArc(sketch, "E175.0", {"start": v(-97.15, 56.72) * mm, "mid": v(-115.36, 61.68) * mm, "end": v(-133.94, 65.04) * mm});
            skArc(sketch, "E176.0", {"start": v(-133.67, 65) * mm, "mid": v(-134.67, 66) * mm, "end": v(-133.67, 67) * mm});
            skArc(sketch, "E177.0", {"start": v(-192.33, 65) * mm, "mid": v(-191.33, 66) * mm, "end": v(-192.33, 67) * mm});
            skLineSegment(sketch, "E178.0", {"start": v(-97.15, 56.72) * mm, "end": v(-97.15, 67) * mm});
            skLineSegment(sketch, "E179.0", {"start": v(-91.15, 67) * mm, "end": v(-91.15, 54.7) * mm});
            skLineSegment(sketch, "E180.0", {"start": v(-91.15, 54.7) * mm, "end": v(-83.47, 67) * mm});
            skLineSegment(sketch, "E181.0", {"start": v(-76.4, 67) * mm, "end": v(-85.4, 52.58) * mm});
            skLineSegment(sketch, "E182.0", {"start": v(-76.4, 48.88) * mm, "end": v(-76.4, 67) * mm});
            skLineSegment(sketch, "E183.0", {"start": v(-70.4, 46.14) * mm, "end": v(-70.4, 67) * mm});
            skLineSegment(sketch, "E184.0", {"start": v(-57.36, 67) * mm, "end": v(-70.4, 46.14) * mm});
            skArc(sketch, "E185.0", {"start": v(-76.4, 48.88) * mm, "mid": v(-80.87, 50.78) * mm, "end": v(-85.4, 52.58) * mm});
            skLineSegment(sketch, "E186.0", {"start": v(-50.28, 67) * mm, "end": v(-64.98, 43.48) * mm});
            skLineSegment(sketch, "E187.0", {"start": v(-50.28, 35.27) * mm, "end": v(-50.28, 67) * mm});
            skArc(sketch, "E188.0", {"start": v(-50.28, 35.27) * mm, "mid": v(-57.55, 39.52) * mm, "end": v(-64.98, 43.48) * mm});
            skLineSegment(sketch, "E189.0", {"start": v(-44.28, 67) * mm, "end": v(-44.28, 31.46) * mm});
            skLineSegment(sketch, "E190.0", {"start": v(-44.28, 31.46) * mm, "end": v(-22.08, 67) * mm});
            skLineSegment(sketch, "E191.0", {"start": v(-15, 67) * mm, "end": v(-39.31, 28.1) * mm});
            skArc(sketch, "E192.0", {"start": v(-15, 8.34) * mm, "mid": v(-26.8, 18.66) * mm, "end": v(-39.31, 28.1) * mm});
            skLineSegment(sketch, "E193.0", {"start": v(-15, 8.34) * mm, "end": v(-15, 67) * mm});
            skLineSegment(sketch, "E194.0", {"start": v(-9, 67) * mm, "end": v(-9, 8.34) * mm});
            skLineSegment(sketch, "E195.0", {"start": v(9, 8.34) * mm, "end": v(9, 67) * mm});
            skLineSegment(sketch, "E196.0", {"start": v(-9, 8.34) * mm, "end": v(9, 8.34) * mm});
            skLineSegment(sketch, "E197.0", {"start": v(-15, 0) * mm, "end": v(15, 0) * mm});
            skLineSegment(sketch, "E198.0", {"start": v(15, 67) * mm, "end": v(39.31, 28.1) * mm});
            skLineSegment(sketch, "E199.0", {"start": v(15, 8.34) * mm, "end": v(15, 67) * mm});
            skArc(sketch, "E200.0", {"start": v(15, 8.34) * mm, "mid": v(26.8, 18.66) * mm, "end": v(39.31, 28.1) * mm});
            skLineSegment(sketch, "E201.0", {"start": v(44.28, 31.46) * mm, "end": v(22.08, 67) * mm});
            skLineSegment(sketch, "E202.0", {"start": v(44.28, 67) * mm, "end": v(44.28, 31.46) * mm});
            skLineSegment(sketch, "E203.0", {"start": v(50.28, 35.27) * mm, "end": v(50.28, 67) * mm});
            skLineSegment(sketch, "E204.0", {"start": v(50.28, 67) * mm, "end": v(64.98, 43.48) * mm});
            skLineSegment(sketch, "E205.0", {"start": v(57.36, 67) * mm, "end": v(70.4, 46.14) * mm});
            skArc(sketch, "E206.0", {"start": v(50.28, 35.27) * mm, "mid": v(57.55, 39.52) * mm, "end": v(64.98, 43.48) * mm});
            skArc(sketch, "E207.0", {"start": v(15, 0) * mm, "mid": v(163, 61) * mm, "end": v(311, 0) * mm});
            skLineSegment(sketch, "E208.0", {"start": v(70.4, 46.14) * mm, "end": v(70.4, 67) * mm});
            skLineSegment(sketch, "E209.0", {"start": v(76.4, 48.88) * mm, "end": v(76.4, 67) * mm});
            skLineSegment(sketch, "E210.0", {"start": v(76.4, 67) * mm, "end": v(85.4, 52.58) * mm});
            skArc(sketch, "E211.0", {"start": v(76.4, 48.88) * mm, "mid": v(80.87, 50.78) * mm, "end": v(85.4, 52.58) * mm});
            skLineSegment(sketch, "E212.0", {"start": v(91.15, 54.7) * mm, "end": v(83.47, 67) * mm});
            skLineSegment(sketch, "E213.0", {"start": v(91.15, 67) * mm, "end": v(91.15, 54.7) * mm});
            skLineSegment(sketch, "E214.0", {"start": v(97.15, 56.72) * mm, "end": v(97.15, 67) * mm});
            skArc(sketch, "E215.0", {"start": v(97.15, 56.72) * mm, "mid": v(115.36, 61.68) * mm, "end": v(133.94, 65.04) * mm});
            skArc(sketch, "E216.0", {"start": v(133.67, 65) * mm, "mid": v(134.67, 66) * mm, "end": v(133.67, 67) * mm});
            skArc(sketch, "E217.0", {"start": v(192.06, 65.04) * mm, "mid": v(210.64, 61.68) * mm, "end": v(228.85, 56.72) * mm});
            skArc(sketch, "E218.0", {"start": v(192.33, 65) * mm, "mid": v(191.33, 66) * mm, "end": v(192.33, 67) * mm});
            skLineSegment(sketch, "E219.0", {"start": v(228.85, 56.72) * mm, "end": v(228.85, 67) * mm});
            skLineSegment(sketch, "E220.0", {"start": v(234.85, 67) * mm, "end": v(234.85, 54.7) * mm});
            skLineSegment(sketch, "E221.0", {"start": v(234.85, 54.7) * mm, "end": v(242.53, 67) * mm});
            skLineSegment(sketch, "E222.0", {"start": v(249.6, 67) * mm, "end": v(240.6, 52.58) * mm});
            skLineSegment(sketch, "E223.0", {"start": v(249.6, 48.88) * mm, "end": v(249.6, 67) * mm});
            skArc(sketch, "E224.0", {"start": v(240.6, 52.58) * mm, "mid": v(245.13, 50.78) * mm, "end": v(249.6, 48.88) * mm});
            skLineSegment(sketch, "E225.0", {"start": v(255.6, 46.14) * mm, "end": v(255.6, 67) * mm});
            skLineSegment(sketch, "E226.0", {"start": v(268.64, 67) * mm, "end": v(255.6, 46.14) * mm});
            skLineSegment(sketch, "E227.0", {"start": v(275.72, 67) * mm, "end": v(261.02, 43.48) * mm});
            skLineSegment(sketch, "E228.0", {"start": v(275.72, 35.27) * mm, "end": v(275.72, 67) * mm});
            skArc(sketch, "E229.0", {"start": v(261.02, 43.48) * mm, "mid": v(268.45, 39.52) * mm, "end": v(275.72, 35.27) * mm});
            skLineSegment(sketch, "E230.0", {"start": v(281.72, 67) * mm, "end": v(281.72, 31.46) * mm});
            skLineSegment(sketch, "E231.0", {"start": v(281.72, 31.46) * mm, "end": v(303.92, 67) * mm});
            skLineSegment(sketch, "E232.0", {"start": v(311, 67) * mm, "end": v(286.69, 28.1) * mm});
            skLineSegment(sketch, "E233.0", {"start": v(311, 8.34) * mm, "end": v(311, 67) * mm});
            skArc(sketch, "E234.0", {"start": v(286.69, 28.1) * mm, "mid": v(299.2, 18.66) * mm, "end": v(311, 8.34) * mm});
            skLineSegment(sketch, "E235.0", {"start": v(331, 0) * mm, "end": v(331, 103.5) * mm});
            skLineSegment(sketch, "E236.0", {"start": v(-331, 0) * mm, "end": v(-331, 103.5) * mm});
            skLineSegment(sketch, "E237.0", {"start": v(-303.92, 67) * mm, "end": v(-281.72, 67) * mm});
            skLineSegment(sketch, "E238", {"start": v(-268.64, 67) * mm, "end": v(-255.6, 67) * mm});
            skLineSegment(sketch, "E239", {"start": v(-242.53, 67) * mm, "end": v(-234.85, 67) * mm});
            skLineSegment(sketch, "E240", {"start": v(-228.85, 67) * mm, "end": v(-192.33, 67) * mm});
            skLineSegment(sketch, "E241", {"start": v(-133.67, 67) * mm, "end": v(-97.15, 67) * mm});
            skLineSegment(sketch, "E242", {"start": v(-91.15, 67) * mm, "end": v(-83.47, 67) * mm});
            skLineSegment(sketch, "E243", {"start": v(-70.4, 67) * mm, "end": v(-57.36, 67) * mm});
            skLineSegment(sketch, "E244", {"start": v(-44.28, 67) * mm, "end": v(-22.08, 67) * mm});
            skLineSegment(sketch, "E245", {"start": v(-9, 67) * mm, "end": v(9, 67) * mm});
            skLineSegment(sketch, "E246", {"start": v(22.08, 67) * mm, "end": v(44.28, 67) * mm});
            skLineSegment(sketch, "E247", {"start": v(70.4, 67) * mm, "end": v(57.36, 67) * mm});
            skLineSegment(sketch, "E248", {"start": v(83.47, 67) * mm, "end": v(91.15, 67) * mm});
            skLineSegment(sketch, "E249", {"start": v(97.15, 67) * mm, "end": v(133.67, 67) * mm});
            skLineSegment(sketch, "E250", {"start": v(192.33, 67) * mm, "end": v(228.85, 67) * mm});
            skLineSegment(sketch, "E251", {"start": v(234.85, 67) * mm, "end": v(242.53, 67) * mm});
            skLineSegment(sketch, "E252", {"start": v(255.6, 67) * mm, "end": v(268.64, 67) * mm});
            skLineSegment(sketch, "E253", {"start": v(281.72, 67) * mm, "end": v(303.92, 67) * mm});
            skArc(sketch, "E254", {"start": v(-258, 103.5) * mm, "mid": v(-294.5, 140) * mm, "end": v(-331, 103.5) * mm});
            skLineSegment(sketch, "E255", {"start": v(-243, 82) * mm, "end": v(243, 82) * mm});
            skArc(sketch, "E256", {"start": v(331, 103.5) * mm, "mid": v(294.5, 140) * mm, "end": v(258, 103.5) * mm});
            skLineSegment(sketch, "E257", {"start": v(258, 97) * mm, "end": v(258, 103.5) * mm});
            skLineSegment(sketch, "E258", {"start": v(-258, 97) * mm, "end": v(-258, 103.5) * mm});
            skPoint(sketch, "E259.visualSharp", {"position": v(-258, 82) * mm});
            skArc(sketch, "E259.filletArc", {"start": v(-258, 97) * mm, "mid": v(-253.6, 86.4) * mm, "end": v(-243, 82) * mm});
            skArc(sketch, "E260", {"start": v(243, 82) * mm, "mid": v(253.6, 86.4) * mm, "end": v(258, 97) * mm});
            skPoint(sketch, "E261.orphan", {"position": v(28, 0) * mm});
            skPoint(sketch, "E262.0.start.orphan", {"position": v(331, 0) * mm});
            skLineSegment(sketch, "E263", {"start": v(311, 0) * mm, "end": v(331, 0) * mm});
            skCircle(sketch, "E264", {"center": v(-294.5, 103.5) * mm, "radius": 5 * mm});
            skCircle(sketch, "E265", {"center": v(294.5, 103.5) * mm, "radius": 9.25 * mm});
            skCircle(sketch, "E266", {"center": v(-273, 103.5) * mm, "radius": 2.5 * mm});
            skCircle(sketch, "E267", {"center": v(-316, 103.5) * mm, "radius": 2.5 * mm});
            skLineSegment(sketch, "E268", {"start": v(-331, 103.5) * mm, "end": v(-258, 103.5) * mm, "construction": true});
            skCircle(sketch, "E269.0", {"center": v(273, 103.5) * mm, "radius": 2.5 * mm});
            skCircle(sketch, "E269.1", {"center": v(316, 103.5) * mm, "radius": 2.5 * mm});
            skSolve(sketch);
        }
        {
            var Q0;
            Q0 = qSketchRegion(id + "F10", true);
            extrude(context, id + "F11", {"entities" : qUnion([Q0]), "depth" : 6 * mm});
        }
        {
            var Q0;
            Q0=makeQuery(id+"F9.opExtrude","SWEPT_FACE",FACE,{"disambiguationData":[OSD([sQuery(id+"F8.wireOp",EDGE,"E151.3")])]});
            var sketch = newSketch(context, id + "F12", { "sketchPlane" : qUnion([Q0])});
            skLineSegment(sketch, "E270.bottom", {"start": v(-294.5, -75) * mm, "end": v(-269.5, -75) * mm});
            skLineSegment(sketch, "E270.top", {"start": v(-294.5, -11) * mm, "end": v(-269.5, -11) * mm});
            skLineSegment(sketch, "E270.left", {"start": v(-294.5, -75) * mm, "end": v(-294.5, -11) * mm});
            skLineSegment(sketch, "E270.right", {"start": v(-269.5, -75) * mm, "end": v(-269.5, -11) * mm});
            skCircle(sketch, "E271", {"center": v(-282, -40.8) * mm, "radius": 2.25 * mm});
            skCircle(sketch, "E272", {"center": v(-282, -66.2) * mm, "radius": 2.25 * mm});
            skLineSegment(sketch, "E273", {"start": v(-282, -11) * mm, "end": v(-282, -75) * mm, "construction": true});
            skLineSegment(sketch, "E274", {"start": v(-294.5, -53.5) * mm, "end": v(-269.5, -53.5) * mm, "construction": true});
            skSolve(sketch);
        }
        {
            var Q0;
            Q0 = qSketchRegion(id + "F12", true);
            extrude(context, id + "F13", {"entities" : qUnion([Q0]), "depth" : 4 * mm});
        }
        {
            var Q0;
            Q0=makeQuery(id+"F2.opExtrude","CAP_FACE",FACE,{"disambiguationData":[OSD([sQuery(id+"F1.wireOp",EDGE,"E14.right"),sQuery(id+"F1.wireOp",EDGE,"E15"),sQuery(id+"F1.wireOp",EDGE,"E16"),sQuery(id+"F1.wireOp",EDGE,"E17"),sQuery(id+"F1.wireOp",EDGE,"E18"),sQuery(id+"F1.wireOp",EDGE,"E19"),sQuery(id+"F1.wireOp",EDGE,"E20"),sQuery(id+"F1.wireOp",EDGE,"E21"),sQuery(id+"F1.wireOp",EDGE,"E33"),sQuery(id+"F1.wireOp",EDGE,"E34"),sQuery(id+"F1.wireOp",EDGE,"E35"),sQuery(id+"F1.wireOp",EDGE,"E36.trimOffspring"),sQuery(id+"F1.wireOp",EDGE,"E37"),sQuery(id+"F1.wireOp",EDGE,"E39"),sQuery(id+"F1.wireOp",EDGE,"E40"),sQuery(id+"F1.wireOp",EDGE,"E41"),sQuery(id+"F1.wireOp",EDGE,"15889549-e419-449c-aa3d-56b1cea7559d")])],"isStart":false});
            var sketch = newSketch(context, id + "F14", { "sketchPlane" : qUnion([Q0])});
            skCircle(sketch, "E275", {"center": v(104.5, 123) * mm, "radius": 5 * mm});
            skSolve(sketch);
        }
        {
            var Q0;
            Q0 = qSketchRegion(id + "F14", true);
            var Q1;
            Q1=makeQuery(id+"F6.opExtrude","CAP_FACE",FACE,{"disambiguationData":[OSD([sQuery(id+"F5.wireOp",EDGE,"E76.0.0"),sQuery(id+"F5.wireOp",EDGE,"E76.0.1"),sQuery(id+"F5.wireOp",EDGE,"E77.0"),sQuery(id+"F5.wireOp",EDGE,"E77.1"),sQuery(id+"F5.wireOp",EDGE,"E77.2"),sQuery(id+"F5.wireOp",EDGE,"E78.0.2"),sQuery(id+"F5.wireOp",EDGE,"E78.0.3"),sQuery(id+"F5.wireOp",EDGE,"E79.0"),sQuery(id+"F5.wireOp",EDGE,"E79.1"),sQuery(id+"F5.wireOp",EDGE,"E79.2"),sQuery(id+"F5.wireOp",EDGE,"E80"),sQuery(id+"F5.wireOp",EDGE,"E86"),sQuery(id+"F5.wireOp",EDGE,"E142"),sQuery(id+"F5.wireOp",EDGE,"E143"),sQuery(id+"F5.wireOp",EDGE,"E144")])],"isStart":true});
            extrude(context, id + "F15", {"entities" : qUnion([Q0]), "endBound" : BoundingType.UP_TO_SURFACE, "endBoundEntityFace" : qUnion([Q1]), "depth" : 25 * mm});
        }
        {
            var Q0;
            Q0=makeQuery(id+"F15.opExtrude","CAP_FACE",FACE,{"disambiguationData":[OSD([sQuery(id+"F14.wireOp",EDGE,"E275")])],"isStart":false});
            var sketch = newSketch(context, id + "F16", { "sketchPlane" : qUnion([Q0])});
            skCircle(sketch, "E276.0", {"center": v(104.5, 123) * mm, "radius": 2.5 * mm});
            skSolve(sketch);
        }
        {
            var Q0;
            Q0 = qSketchRegion(id + "F16", true);
            var Q1;
            Q1=makeQuery(id+"F6.opExtrude","CAP_FACE",FACE,{"disambiguationData":[OSD([sQuery(id+"F5.wireOp",EDGE,"E76.0.0"),sQuery(id+"F5.wireOp",EDGE,"E76.0.1"),sQuery(id+"F5.wireOp",EDGE,"E77.0"),sQuery(id+"F5.wireOp",EDGE,"E77.1"),sQuery(id+"F5.wireOp",EDGE,"E77.2"),sQuery(id+"F5.wireOp",EDGE,"E78.0.2"),sQuery(id+"F5.wireOp",EDGE,"E78.0.3"),sQuery(id+"F5.wireOp",EDGE,"E79.0"),sQuery(id+"F5.wireOp",EDGE,"E79.1"),sQuery(id+"F5.wireOp",EDGE,"E79.2"),sQuery(id+"F5.wireOp",EDGE,"E80"),sQuery(id+"F5.wireOp",EDGE,"E86"),sQuery(id+"F5.wireOp",EDGE,"E142"),sQuery(id+"F5.wireOp",EDGE,"E143"),sQuery(id+"F5.wireOp",EDGE,"E144")])],"isStart":false});
            extrude(context, id + "F17", {"entities" : qUnion([Q0]), "operationType" : NewBodyOperationType.ADD, "endBound" : BoundingType.UP_TO_SURFACE, "endBoundEntityFace" : qUnion([Q1]), "depth" : 25 * mm});
        }
        {
            var Q0;
            Q0=makeQuery(id+"F15.opExtrude","CAP_FACE",FACE,{"disambiguationData":[OSD([sQuery(id+"F14.wireOp",EDGE,"E275")])],"isStart":true});
            var sketch = newSketch(context, id + "F18", { "sketchPlane" : qUnion([Q0])});
            skCircle(sketch, "E277.0", {"center": v(-104.5, 123) * mm, "radius": 2.5 * mm});
            skSolve(sketch);
        }
        {
            var Q0;
            Q0 = qSketchRegion(id + "F18", true);
            var Q1;
            Q1=makeQuery(id+"F2.opExtrude","CAP_FACE",FACE,{"disambiguationData":[OSD([sQuery(id+"F1.wireOp",EDGE,"E14.right"),sQuery(id+"F1.wireOp",EDGE,"E15"),sQuery(id+"F1.wireOp",EDGE,"E16"),sQuery(id+"F1.wireOp",EDGE,"E17"),sQuery(id+"F1.wireOp",EDGE,"E18"),sQuery(id+"F1.wireOp",EDGE,"E19"),sQuery(id+"F1.wireOp",EDGE,"E20"),sQuery(id+"F1.wireOp",EDGE,"E21"),sQuery(id+"F1.wireOp",EDGE,"E33"),sQuery(id+"F1.wireOp",EDGE,"E34"),sQuery(id+"F1.wireOp",EDGE,"E35"),sQuery(id+"F1.wireOp",EDGE,"E36.trimOffspring"),sQuery(id+"F1.wireOp",EDGE,"E37"),sQuery(id+"F1.wireOp",EDGE,"E39"),sQuery(id+"F1.wireOp",EDGE,"E40"),sQuery(id+"F1.wireOp",EDGE,"E41"),sQuery(id+"F1.wireOp",EDGE,"15889549-e419-449c-aa3d-56b1cea7559d")])],"isStart":true});
            extrude(context, id + "F19", {"entities" : qUnion([Q0]), "operationType" : NewBodyOperationType.ADD, "endBound" : BoundingType.UP_TO_SURFACE, "endBoundEntityFace" : qUnion([Q1]), "depth" : 25 * mm});
        }
        {
            var Q0;
            Q0=makeQuery(id+"F2.opExtrude","SWEPT_FACE",FACE,{"disambiguationData":[OSD([sQuery(id+"F1.wireOp",EDGE,"E51.0.MirrorCS")])]});
            var sketch = newSketch(context, id + "F20", { "sketchPlane" : qUnion([Q0])});
            skLineSegment(sketch, "E278", {"start": v(90, 34.48) * mm, "end": v(90, 0) * mm});
            skLineSegment(sketch, "E279", {"start": v(90, 0) * mm, "end": v(0, 0) * mm});
            skLineSegment(sketch, "E280", {"start": v(0, 0) * mm, "end": v(0, 30) * mm});
            skLineSegment(sketch, "E281", {"start": v(0, 30) * mm, "end": v(-6, 30) * mm});
            skLineSegment(sketch, "E282", {"start": v(-6, 30) * mm, "end": v(-6, 90) * mm});
            skLineSegment(sketch, "E283", {"start": v(-6, 90) * mm, "end": v(0, 90) * mm});
            skLineSegment(sketch, "E284", {"start": v(0, 90) * mm, "end": v(0, 110) * mm});
            skLineSegment(sketch, "E285", {"start": v(0, 110) * mm, "end": v(90, 34.48) * mm});
            skSolve(sketch);
        }
        {
            var Q0;
            Q0 = qSketchRegion(id + "F20", true);
            extrude(context, id + "F21", {"entities" : qUnion([Q0]), "depth" : 6 * mm});
        }
        {
            var Q0;
            Q0=makeQuery(id+"F21.opExtrude","CAP_FACE",FACE,{"disambiguationData":[OSD([sQuery(id+"F1.wireOp",EDGE,"E51.0.MirrorCS"),sQuery(id+"F20.wireOp",EDGE,"E278"),sQuery(id+"F20.wireOp",EDGE,"E279"),sQuery(id+"F20.wireOp",EDGE,"E280"),sQuery(id+"F20.wireOp",EDGE,"E284"),sQuery(id+"F20.wireOp",EDGE,"E285")])],"isStart":true});
            var Q1;
            Q1=makeQuery(id+"F2.opExtrude","SWEPT_FACE",FACE,{"disambiguationData":[OSD([sQuery(id+"F1.wireOp",EDGE,"E47.left")])]});
            cPlane(context, id + "F22", {"entities" : qUnion([Q0, Q1]), "cplaneType" : CPlaneType.MID_PLANE, "offset" : 150 * mm, "width" : 150 * mm, "height" : 150 * mm});
        }
        {
            var Q0;
            Q0=makeQuery(id+"F21.opExtrude","SWEPT_BODY",BODY,{"disambiguationData":[OSD([sQuery(id+"F1.wireOp",EDGE,"E51.0.MirrorCS"),sQuery(id+"F20.wireOp",EDGE,"E278"),sQuery(id+"F20.wireOp",EDGE,"E279"),sQuery(id+"F20.wireOp",EDGE,"E280"),sQuery(id+"F20.wireOp",EDGE,"E284"),sQuery(id+"F20.wireOp",EDGE,"E285")])]});
            var Q1;
            Q1=qCreatedBy(id+"F22.planeOp",FACE);
            mirror(context, id + "F23", {"entities" : qUnion([Q0]), "mirrorPlane" : qUnion([Q1])});
        }
        {
            var Q0;
            Q0=makeQuery(id+"F13.opExtrude","CAP_FACE",FACE,{"disambiguationData":[OSD([sQuery(id+"F12.wireOp",EDGE,"E270.bottom"),sQuery(id+"F12.wireOp",EDGE,"E270.top"),sQuery(id+"F12.wireOp",EDGE,"E270.left"),sQuery(id+"F12.wireOp",EDGE,"E270.right"),sQuery(id+"F12.wireOp",EDGE,"E271"),sQuery(id+"F12.wireOp",EDGE,"E272")])],"isStart":false});
            var sketch = newSketch(context, id + "F24", { "sketchPlane" : qUnion([Q0])});
            skLineSegment(sketch, "E286.bottom", {"start": v(-309.5, -15) * mm, "end": v(-294.5, -15) * mm});
            skLineSegment(sketch, "E286.top", {"start": v(-309.5, -70) * mm, "end": v(-294.5, -70) * mm});
            skLineSegment(sketch, "E286.left", {"start": v(-309.5, -15) * mm, "end": v(-309.5, -30) * mm});
            skLineSegment(sketch, "E286.right", {"start": v(-254.5, -15) * mm, "end": v(-254.5, -30) * mm});
            skLineSegment(sketch, "E287", {"start": v(-282, -40.8) * mm, "end": v(-282, -66.2) * mm, "construction": true});
            skLineSegment(sketch, "E288", {"start": v(-282, -15) * mm, "end": v(-282, -70) * mm, "construction": true});
            skCircle(sketch, "E289.0", {"center": v(-282, -40.8) * mm, "radius": 2.25 * mm});
            skCircle(sketch, "E289.1", {"center": v(-282, -66.2) * mm, "radius": 2.25 * mm});
            skLineSegment(sketch, "E290", {"start": v(-294.5, -70) * mm, "end": v(-294.5, -74) * mm});
            skLineSegment(sketch, "E291", {"start": v(-294.5, -74) * mm, "end": v(-269.5, -74) * mm});
            skLineSegment(sketch, "E292", {"start": v(-269.5, -74) * mm, "end": v(-269.5, -70) * mm});
            skLineSegment(sketch, "E293.trimOffspring", {"start": v(-269.5, -70) * mm, "end": v(-254.5, -70) * mm});
            skLineSegment(sketch, "E294", {"start": v(-309.5, -42.5) * mm, "end": v(-254.5, -42.5) * mm, "construction": true});
            skLineSegment(sketch, "E295.0.MirrorCS", {"start": v(-294.5, -11) * mm, "end": v(-269.5, -11) * mm});
            skLineSegment(sketch, "E296.0.MirrorCS", {"start": v(-294.5, -15) * mm, "end": v(-294.5, -11) * mm});
            skLineSegment(sketch, "E297.0.MirrorCS", {"start": v(-269.5, -11) * mm, "end": v(-269.5, -15) * mm});
            skLineSegment(sketch, "E298.trimOffspring", {"start": v(-269.5, -15) * mm, "end": v(-254.5, -15) * mm});
            skLineSegment(sketch, "E299", {"start": v(-309.5, -30) * mm, "end": v(-313.5, -30) * mm});
            skLineSegment(sketch, "E300", {"start": v(-313.5, -30) * mm, "end": v(-313.5, -55) * mm});
            skLineSegment(sketch, "E301", {"start": v(-313.5, -55) * mm, "end": v(-309.5, -55) * mm});
            skLineSegment(sketch, "E302.trimOffspring", {"start": v(-309.5, -55) * mm, "end": v(-309.5, -70) * mm});
            skLineSegment(sketch, "E303.0.MirrorCS", {"start": v(-254.5, -30) * mm, "end": v(-250.5, -30) * mm});
            skLineSegment(sketch, "E304.0.MirrorCS", {"start": v(-250.5, -30) * mm, "end": v(-250.5, -55) * mm});
            skLineSegment(sketch, "E305.0.MirrorCS", {"start": v(-250.5, -55) * mm, "end": v(-254.5, -55) * mm});
            skLineSegment(sketch, "E306.trimOffspring", {"start": v(-254.5, -55) * mm, "end": v(-254.5, -70) * mm});
            skSolve(sketch);
        }
        {
            var Q0;
            Q0 = qSketchRegion(id + "F24", true);
            extrude(context, id + "F25", {"entities" : qUnion([Q0]), "depth" : 4 * mm});
        }
        {
            var Q0;
            Q0=makeQuery(id+"F4.opExtrude","SWEPT_FACE",FACE,{"disambiguationData":[OSD([sQuery(id+"F3.wireOp",EDGE,"E74.bottom")])]});
            var sketch = newSketch(context, id + "F26", { "sketchPlane" : qUnion([Q0])});
            skLineSegment(sketch, "E307.bottom", {"start": v(-207.95, -6) * mm, "end": v(-177.95, -6) * mm});
            skLineSegment(sketch, "E307.top", {"start": v(-207.95, -71) * mm, "end": v(-195.95, -71) * mm});
            skLineSegment(sketch, "E307.left", {"start": v(-207.95, -6) * mm, "end": v(-207.95, -71) * mm});
            skLineSegment(sketch, "E307.right", {"start": v(-177.95, -6) * mm, "end": v(-177.95, -71) * mm});
            skLineSegment(sketch, "E308.top", {"start": v(-195.95, -38.5) * mm, "end": v(-189.95, -38.5) * mm});
            skLineSegment(sketch, "E308.left", {"start": v(-195.95, -71) * mm, "end": v(-195.95, -38.5) * mm});
            skLineSegment(sketch, "E308.right", {"start": v(-189.95, -71) * mm, "end": v(-189.95, -38.5) * mm});
            skLineSegment(sketch, "E309.trimOffspring", {"start": v(-189.95, -71) * mm, "end": v(-177.95, -71) * mm});
            skSolve(sketch);
        }
        {
            var Q0;
            Q0=makeQuery(id+"F26.imprint","IMPRINT",FACE,{"disambiguationData":[TD([[makeQuery(id+"F26.imprint","IMPRINT",EDGE,{"derivedFrom":sQuery(id+"F26.wireOp",EDGE,"E307.bottom")}),-1.0]])]});
            extrude(context, id + "F27", {"entities" : qUnion([Q0]), "depth" : 6 * mm});
        }
        {
            var Q0;
            Q0=makeQuery(id+"F25.opExtrude","SWEPT_FACE",FACE,{"disambiguationData":[OSD([sQuery(id+"F24.wireOp",EDGE,"E291")])]});
            var Q1;
            Q1=makeQuery(id+"F25.opExtrude","SWEPT_FACE",FACE,{"disambiguationData":[OSD([sQuery(id+"F24.wireOp",EDGE,"E295.0.MirrorCS")])]});
            cPlane(context, id + "F28", {"entities" : qUnion([Q0, Q1]), "cplaneType" : CPlaneType.MID_PLANE, "offset" : 150 * mm, "width" : 150 * mm, "height" : 150 * mm});
        }
        {
            var Q0;
            Q0=makeQuery(id+"F25.opExtrude","SWEPT_FACE",FACE,{"disambiguationData":[OSD([sQuery(id+"F24.wireOp",EDGE,"E286.right")])]});
            var Q1;
            Q1=makeQuery(id+"F25.opExtrude","SWEPT_FACE",FACE,{"disambiguationData":[OSD([sQuery(id+"F24.wireOp",EDGE,"E286.left")])]});
            cPlane(context, id + "F29", {"entities" : qUnion([Q0, Q1]), "cplaneType" : CPlaneType.MID_PLANE, "offset" : 150 * mm, "width" : 150 * mm, "height" : 150 * mm});
        }
        {
            var Q0;
            Q0=qCreatedBy(id+"F29.planeOp",FACE);
            var sketch = newSketch(context, id + "F30", { "sketchPlane" : qUnion([Q0])});
            skLineSegment(sketch, "E310", {"start": v(-7, 189) * mm, "end": v(-76, 189) * mm, "construction": true});
            skLineSegment(sketch, "E311", {"start": v(-76, 189) * mm, "end": v(-74, 144) * mm, "construction": true});
            skLineSegment(sketch, "E312", {"start": v(-74, 144) * mm, "end": v(-11, 144) * mm, "construction": true});
            skLineSegment(sketch, "E313", {"start": v(-11, 144) * mm, "end": v(-7, 189) * mm, "construction": true});
            skLineSegment(sketch, "E314", {"start": v(-6, 189) * mm, "end": v(-6, 140) * mm, "construction": true});
            skLineSegment(sketch, "E315", {"start": v(-77, 189) * mm, "end": v(-77, 140) * mm, "construction": true});
            skSolve(sketch);
        }
        {
            var Q0;
            Q0=makeQuery(id+"F25.opExtrude","CAP_VERTEX",VERTEX,{"disambiguationData":[OSD([sQuery(id+"F24.wireOp",EDGE,"E295.0.MirrorCS"),sQuery(id+"F24.wireOp",EDGE,"E296.0.MirrorCS")])],"isStart":true});
            var Q1;
            Q1=makeQuery(id+"F25.opExtrude","CAP_VERTEX",VERTEX,{"disambiguationData":[OSD([sQuery(id+"F24.wireOp",EDGE,"E295.0.MirrorCS"),sQuery(id+"F24.wireOp",EDGE,"E297.0.MirrorCS")])],"isStart":true});
            var Q2;
            Q2=sQuery(id+"F30.wireOp",VERTEX,"E313.end");
            cPlane(context, id + "F31", {"entities" : qUnion([Q0, Q1, Q2]), "cplaneType" : CPlaneType.THREE_POINT, "offset" : 150 * mm, "width" : 150 * mm, "height" : 150 * mm});
        }
        {
            var Q0;
            Q0=qCreatedBy(id+"F31.planeOp",FACE);
            var sketch = newSketch(context, id + "F32", { "sketchPlane" : qUnion([Q0])});
            skLineSegment(sketch, "E316", {"start": v(254.5, 142.1) * mm, "end": v(269.5, 142.1) * mm});
            skLineSegment(sketch, "E317", {"start": v(269.5, 142.1) * mm, "end": v(269.5, 146.44) * mm});
            skLineSegment(sketch, "E318", {"start": v(269.5, 146.44) * mm, "end": v(294.5, 146.44) * mm});
            skLineSegment(sketch, "E319", {"start": v(294.5, 146.44) * mm, "end": v(294.5, 142.1) * mm});
            skLineSegment(sketch, "E320", {"start": v(294.5, 142.1) * mm, "end": v(309.5, 142.1) * mm});
            skLineSegment(sketch, "E321", {"start": v(309.5, 142.1) * mm, "end": v(321.56, 187.1) * mm});
            skLineSegment(sketch, "E322", {"start": v(321.56, 187.1) * mm, "end": v(242.44, 187.1) * mm});
            skLineSegment(sketch, "E323", {"start": v(242.44, 187.1) * mm, "end": v(254.5, 142.1) * mm});
            skSolve(sketch);
        }
        {
            var Q0;
            Q0 = qSketchRegion(id + "F32", true);
            extrude(context, id + "F33", {"entities" : qUnion([Q0]), "oppositeDirection" : true, "depth" : 4 * mm});
        }
        {
            var Q0;
            Q0=makeQuery(id+"F33.opExtrude","SWEPT_BODY",BODY,{"disambiguationData":[OSD([sQuery(id+"F32.wireOp",EDGE,"E316"),sQuery(id+"F32.wireOp",EDGE,"E317"),sQuery(id+"F32.wireOp",EDGE,"E318"),sQuery(id+"F32.wireOp",EDGE,"E319"),sQuery(id+"F32.wireOp",EDGE,"E320"),sQuery(id+"F32.wireOp",EDGE,"E321"),sQuery(id+"F32.wireOp",EDGE,"E322"),sQuery(id+"F32.wireOp",EDGE,"E323")])]});
            var Q1;
            Q1=qCreatedBy(id+"F28.planeOp",FACE);
            mirror(context, id + "F34", {"entities" : qUnion([Q0]), "mirrorPlane" : qUnion([Q1])});
        }
        {
            var Q0;
            Q0=makeQuery(id+"F33.opExtrude","CAP_VERTEX",VERTEX,{"disambiguationData":[OSD([sQuery(id+"F32.wireOp",EDGE,"E321"),sQuery(id+"F32.wireOp",EDGE,"E322")])],"isStart":true});
            var Q1;
            Q1=makeQuery(id+"F34.opPattern","COPY",VERTEX,{"derivedFrom":makeQuery(id+"F33.opExtrude","CAP_VERTEX",VERTEX,{"disambiguationData":[OSD([sQuery(id+"F32.wireOp",EDGE,"E321"),sQuery(id+"F32.wireOp",EDGE,"E322")])],"isStart":true}),"instanceName":"1"});
            var Q2;
            Q2=makeQuery(id+"F33.opExtrude","CAP_VERTEX",VERTEX,{"disambiguationData":[OSD([sQuery(id+"F32.wireOp",EDGE,"E320"),sQuery(id+"F32.wireOp",EDGE,"E321")])],"isStart":true});
            cPlane(context, id + "F35", {"entities" : qUnion([Q0, Q1, Q2]), "cplaneType" : CPlaneType.THREE_POINT, "offset" : 150 * mm, "width" : 150 * mm, "height" : 150 * mm});
        }
        {
            var Q0;
            Q0=qCreatedBy(id+"F35.planeOp",FACE);
            var sketch = newSketch(context, id + "F36", { "sketchPlane" : qUnion([Q0])});
            skLineSegment(sketch, "E324", {"start": v(77.95, 265.53) * mm, "end": v(7.05, 265.53) * mm});
            skLineSegment(sketch, "E325", {"start": v(7.05, 265.53) * mm, "end": v(11.03, 219.11) * mm});
            skLineSegment(sketch, "E326", {"start": v(11.03, 219.11) * mm, "end": v(30, 219.11) * mm});
            skLineSegment(sketch, "E327", {"start": v(73.97, 219.11) * mm, "end": v(77.95, 265.53) * mm});
            skLineSegment(sketch, "E328", {"start": v(30, 219.11) * mm, "end": v(30, 224.36) * mm});
            skLineSegment(sketch, "E329", {"start": v(30, 224.36) * mm, "end": v(55, 224.36) * mm});
            skLineSegment(sketch, "E330", {"start": v(55, 224.36) * mm, "end": v(55, 219.11) * mm});
            skLineSegment(sketch, "E331.trimOffspring", {"start": v(55, 219.11) * mm, "end": v(73.97, 219.11) * mm});
            skSolve(sketch);
        }
        {
            var Q0;
            Q0 = qSketchRegion(id + "F36", true);
            extrude(context, id + "F37", {"entities" : qUnion([Q0]), "depth" : 4 * mm});
        }
        {
            var Q0;
            Q0=makeQuery(id+"F37.opExtrude","SWEPT_BODY",BODY,{"disambiguationData":[OSD([sQuery(id+"F36.wireOp",EDGE,"E324"),sQuery(id+"F36.wireOp",EDGE,"E325"),sQuery(id+"F36.wireOp",EDGE,"E326"),sQuery(id+"F36.wireOp",EDGE,"E327"),sQuery(id+"F36.wireOp",EDGE,"E328"),sQuery(id+"F36.wireOp",EDGE,"E329"),sQuery(id+"F36.wireOp",EDGE,"E330"),sQuery(id+"F36.wireOp",EDGE,"E331.trimOffspring")])]});
            var Q1;
            Q1=qCreatedBy(id+"F29.planeOp",FACE);
            mirror(context, id + "F38", {"entities" : qUnion([Q0]), "mirrorPlane" : qUnion([Q1])});
        }
    });
